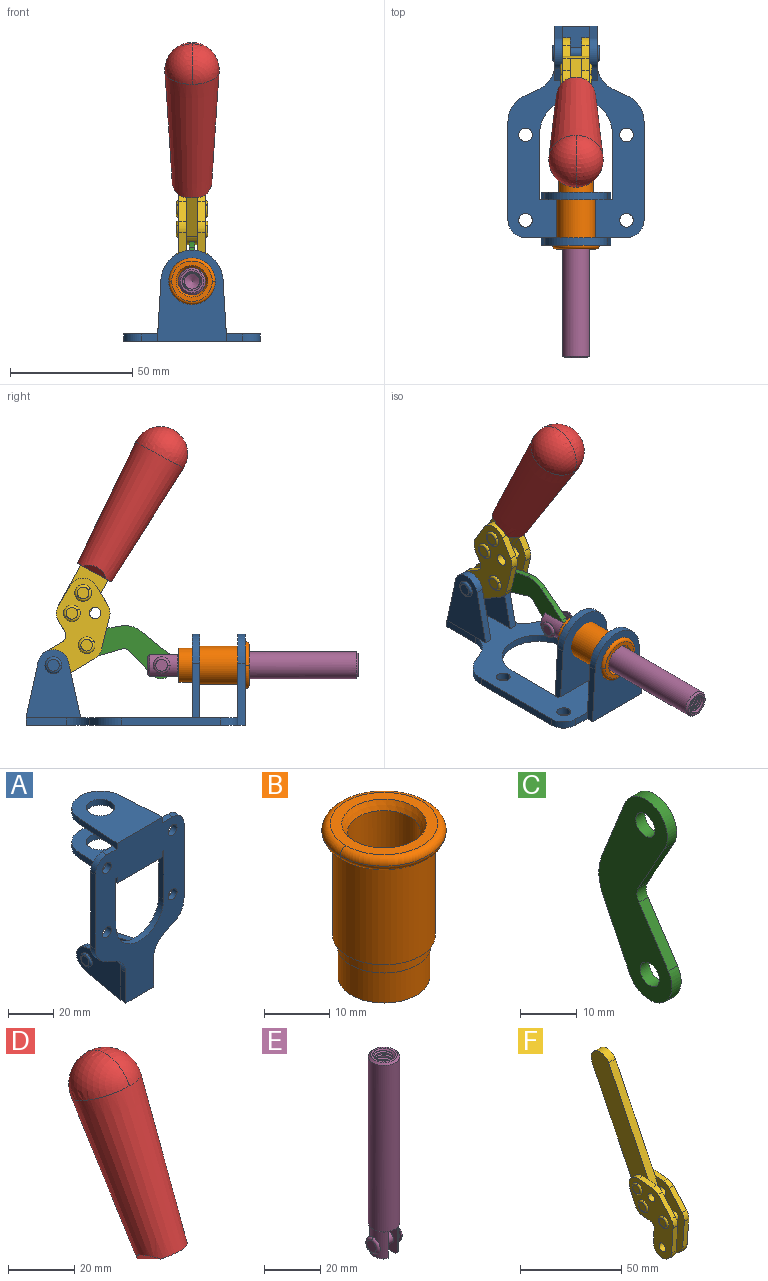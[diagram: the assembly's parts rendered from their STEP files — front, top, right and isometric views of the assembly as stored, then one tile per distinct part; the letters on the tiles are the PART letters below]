
ASSEMBLY  parts=6 mates=6
PART A: 55 faces, bbox 55.7x37.4x89.8 mm
  f0: torus R=2.41mm, axis (-1,0,0), area 15mm2, adj f11,f15,f25
  f1: torus R=2.41mm, axis (-1,0,0), area 15mm2, adj f10,f12,f22
  f2: cylinder r=2.78mm len=5.56mm, axis (0,-1,0), area 54.2mm2, adj f30,f54
  f3: cylinder r=14.99mm len=29.97mm, axis (0,-1,0), area 145.9mm2, adj f30,f49,f53,f54
  f4: cylinder r=2.78mm len=5.56mm, axis (0,-1,0), area 54.2mm2, adj f30,f54
  f5: cylinder r=2.78mm len=5.56mm, axis (0,-1,0), area 54.2mm2, adj f30,f54
  f6: cylinder r=2.78mm len=5.56mm, axis (0,-1,0), area 54.2mm2, adj f30,f54
  f7: cylinder r=6.35mm len=12.7mm, axis (0,0,1), area 123.6mm2, adj f27,f51
  f8: cylinder r=6.35mm len=12.7mm, axis (0,0,-1), area 124.7mm2, adj f21,f35
  f9: cylinder r=2.41mm len=11.18mm, axis (-1,0,0), area 169.4mm2, adj f16,f19
  f10: plane 4.83x4.83mm, normal (1,0,0), area 18.3mm2, adj f1,f12
  f11: plane 4.83x4.83mm, normal (-1,0,0), area 18.3mm2, adj f0,f15
  f12: torus R=2.41mm, axis (-1,0,0), area 15mm2, adj f1,f10,f22
  f13: cylinder r=6.35mm len=12.41mm, axis (1,0,0), area 53.4mm2, adj f18,f19,f22,f23
  f14: cylinder r=6.35mm len=12.41mm, axis (-1,0,0), area 53.4mm2, adj f16,f17,f24,f25
  f15: torus R=2.41mm, axis (-1,0,0), area 15mm2, adj f0,f11,f25
  f16: plane 27.86x22.35mm, normal (1,0,0), area 425.4mm2, adj f9,f14,f17,f24,f30
  f17: plane 22.86x4.97mm, normal (0,0.21,0.98), area 72.5mm2, adj f14,f16,f25,f30
  f18: plane 22.86x4.97mm, normal (0,0.21,0.98), area 72.5mm2, adj f13,f19,f22,f30
  f19: plane 27.86x22.35mm, normal (-1,0,0), area 425.4mm2, adj f9,f13,f18,f23,f30
  f20: cylinder r=12.7mm len=25.35mm, axis (0,0,-1), area 119.8mm2, adj f21,f34,f35,f36
  f21: plane 34.21x28.07mm, normal (0,0,-1), area 702.4mm2, adj f8,f20,f30,f34,f36
  f22: plane 27.96x22.45mm, normal (1,0,0), area 407.2mm2, adj f1,f12,f13,f18,f23,f30,f42,f43
  f23: plane 22.86x4.97mm, normal (0,0.21,-0.98), area 72.5mm2, adj f13,f19,f22,f44
  f24: plane 22.86x4.97mm, normal (0,0.21,-0.98), area 72.5mm2, adj f14,f16,f25,f44
  f25: plane 27.86x22.35mm, normal (-1,0,0), area 407.1mm2, adj f0,f14,f15,f17,f24,f30,f45,f46
  f26: plane 3.1x0.95mm, normal (0,0,-1), area 2.7mm2, adj f30,f49,f50,f54
  f27: plane 34.21x28.07mm, normal (0,0,1), area 702.4mm2, adj f7,f28,f30,f50,f52
  f28: cylinder r=12.7mm len=25.35mm, axis (0,0,1), area 118.8mm2, adj f27,f50,f51,f52
  f29: plane 3.1x0.95mm, normal (0,0,-1), area 2.7mm2, adj f30,f52,f53,f54
  f30: plane 86.54x55.63mm, normal (0,1,0), area 2362.9mm2, adj f2,f3,f4,f5,f6,f16,f17,f18
  f31: plane 40.56x3.1mm, normal (-1,0,0), area 125.7mm2, adj f30,f32,f48,f54
  f32: cylinder r=7.11mm len=7.11mm, axis (0,-1,0), area 34.6mm2, adj f30,f31,f33,f54
  f33: plane 6.67x3.1mm, normal (0,0,1), area 20.4mm2, adj f30,f32,f34,f54
  f34: plane 25.39x3.13mm, normal (-1,0.06,0), area 79.5mm2, adj f20,f21,f33,f35,f54
  f35: plane 37.31x28.45mm, normal (0,0,1), area 789.9mm2, adj f8,f20,f34,f36,f54
  f36: plane 25.39x3.13mm, normal (1,0.06,0), area 79.5mm2, adj f20,f21,f35,f37,f54
  f37: plane 6.67x3.1mm, normal (0,0,1), area 20.4mm2, adj f30,f36,f38,f54
  f38: cylinder r=7.11mm len=7.11mm, axis (0,-1,0), area 34.6mm2, adj f30,f37,f39,f54
  f39: plane 40.56x3.1mm, normal (1,0,0), area 125.7mm2, adj f30,f38,f40,f54
  f40: cylinder r=11.18mm len=10.16mm, axis (0,-1,0), area 39.5mm2, adj f30,f39,f41,f54
  f41: plane 6.09x3.1mm, normal (0.42,0,-0.91), area 20.8mm2, adj f30,f40,f42,f54
  f42: cylinder r=11.18mm len=9.41mm, axis (0,-1,0), area 37.2mm2, adj f22,f30,f41,f43,f54
  f43: plane 16.5x3.1mm, normal (1,0,0), area 51.1mm2, adj f22,f42,f44,f54
  f44: plane 17.37x3.1mm, normal (0,0,-1), area 53.8mm2, adj f23,f24,f30,f43,f45,f54
  f45: plane 16.5x3.1mm, normal (-1,0,0), area 51.1mm2, adj f25,f44,f46,f54
  f46: cylinder r=11.18mm len=9.41mm, axis (0,-1,0), area 37.2mm2, adj f25,f30,f45,f47,f54
  f47: plane 6.09x3.1mm, normal (-0.42,0,-0.91), area 20.8mm2, adj f30,f46,f48,f54
  f48: cylinder r=11.18mm len=10.16mm, axis (0,-1,0), area 39.5mm2, adj f30,f31,f47,f54
  f49: plane 26.54x3.1mm, normal (-1,0,0), area 82.3mm2, adj f3,f26,f30,f54
  f50: plane 25.39x3.1mm, normal (1,0.06,0), area 78.8mm2, adj f26,f27,f28,f51,f54
  f51: plane 37.31x28.45mm, normal (0,0,-1), area 789.9mm2, adj f7,f28,f50,f52,f54
  f52: plane 25.39x3.1mm, normal (-1,0.06,0), area 78.8mm2, adj f27,f28,f29,f51,f54
  f53: plane 26.54x3.1mm, normal (1,0,0), area 82.3mm2, adj f3,f29,f30,f54
  f54: plane 89.66x55.63mm, normal (0,-1,0), area 2678.5mm2, adj f2,f3,f4,f5,f6,f26,f29,f31
PART B: 15 faces, bbox 20.6x20.6x28.7 mm
  f0: torus R=8.26mm, axis (0,0,1), area 56.8mm2, adj f1,f10,f12
  f1: torus R=8.26mm, axis (0,0,1), area 56.8mm2, adj f0,f6,f13
  f2: cylinder r=5.59mm len=25.91mm, axis (0,0,1), area 909.6mm2, adj f3,f4
  f3: cone r=6.86mm half-angle=45deg, axis (0,0,-1), area 70.2mm2, adj f2,f14
  f4: cone r=6.47mm half-angle=30deg, axis (0,0,1), area 66.7mm2, adj f2,f13
  f5: cylinder r=7.04mm len=14.07mm, axis (0,0,1), area 252.6mm2, adj f11,f14
  f6: torus R=8.26mm, axis (0,0,1), area 56.8mm2, adj f1,f12,f13
  f7: cylinder r=7.16mm len=14.33mm, axis (0,0,1), area 91.5mm2, adj f9,f11
  f8: cylinder r=7.86mm len=18.42mm, axis (0,0,1), area 909.6mm2, adj f9,f10
  f9: plane 15.72x15.72mm, normal (0,0,-1), area 33mm2, adj f7,f8
  f10: plane 16.51x16.51mm, normal (0,0,-1), area 19.9mm2, adj f0,f8,f12
  f11: plane 14.33x14.33mm, normal (0,0,-1), area 5.7mm2, adj f5,f7
  f12: torus R=8.26mm, axis (0,0,1), area 56.8mm2, adj f0,f6,f10
  f13: plane 16.51x16.51mm, normal (0,0,1), area 82.7mm2, adj f1,f4,f6
  f14: plane 14.07x14.07mm, normal (0,0,-1), area 7.8mm2, adj f3,f5
PART C: 12 faces, bbox 2.3x18.2x42.8 mm
  f0: cylinder r=2.4mm len=4.8mm, axis (1,0,0), area 34.9mm2, adj f4,f11
  f1: cylinder r=10.41mm len=8.47mm, axis (1,0,0), area 20.2mm2, adj f4,f9,f10,f11
  f2: cylinder r=3.05mm len=3.16mm, axis (1,0,0), area 7.7mm2, adj f4,f6,f7,f11
  f3: cylinder r=2.4mm len=4.8mm, axis (1,0,0), area 34.9mm2, adj f4,f11
  f4: plane 42.81x18.23mm, normal (-1,0,0), area 414.1mm2, adj f0,f1,f2,f3,f5,f6,f7,f8
  f5: cylinder r=5.54mm len=10.67mm, axis (1,0,0), area 41.8mm2, adj f4,f6,f10,f11
  f6: plane 11.66x6.53mm, normal (0,-0.87,-0.49), area 30.9mm2, adj f2,f4,f5,f11
  f7: plane 11.17x7.33mm, normal (0,-0.84,0.55), area 30.9mm2, adj f2,f4,f8,f11
  f8: cylinder r=5.54mm len=10.51mm, axis (1,0,0), area 41.8mm2, adj f4,f7,f9,f11
  f9: plane 13.67x6.67mm, normal (0,0.9,-0.44), area 35.1mm2, adj f1,f4,f8,f11
  f10: plane 14.1x5.7mm, normal (0,0.93,0.37), area 35.1mm2, adj f1,f4,f5,f11
  f11: plane 42.81x18.23mm, normal (1,0,0), area 414.1mm2, adj f0,f1,f2,f3,f5,f6,f7,f8
PART D: 11 faces, bbox 22.3x42.6x64.5 mm
  f0: sphere r=11.13mm, area 411.4mm2, adj f1,f8
  f1: cone r=11.11mm half-angle=3.3deg, axis (0,0.44,0.9), area 3251.8mm2, adj f0,f7,f8,f9,f10
  f2: cylinder r=6.16mm len=11.7mm, axis (1,0,0), area 89.5mm2, adj f3,f4,f5,f6
  f3: plane 60.23x36.75mm, normal (-1,0,0), area 763.6mm2, adj f2,f4,f6,f10
  f4: plane 51.37x25.05mm, normal (0,0.9,-0.44), area 264.2mm2, adj f2,f3,f5,f10
  f5: plane 60.23x36.75mm, normal (1,0,0), area 763.6mm2, adj f2,f4,f6,f10
  f6: plane 51.37x25.05mm, normal (0,-0.9,0.44), area 264.2mm2, adj f2,f3,f5,f10
  f7: plane 9.95x5.95mm, normal (0.71,-0.31,-0.64), area 25.8mm2, adj f1,f10
  f8: sphere r=11.13mm, area 411.4mm2, adj f0,f1
  f9: plane 9.95x5.95mm, normal (-0.71,-0.31,-0.64), area 25.8mm2, adj f1,f10
  f10: plane 14.27x11.38mm, normal (0,-0.44,-0.9), area 106.7mm2, adj f1,f3,f4,f5,f6,f7,f9
PART E: 48 faces, bbox 12.6x11.1x86.1 mm
  f0: torus R=2.41mm, axis (-1,0,0), area 15mm2, adj f30,f32,f34
  f1: torus R=2.41mm, axis (-1,0,0), area 15mm2, adj f29,f31,f33
  f2: cylinder r=5.54mm len=72.39mm, axis (0,0,1), area 2518.5mm2, adj f3,f4,f42,f43
  f3: cone r=5.54mm half-angle=45deg, axis (0,0,1), area 7.6mm2, adj f2,f5,f41
  f4: cone r=5.54mm half-angle=45deg, axis (0,0,-1), area 34.9mm2, adj f2,f39
  f5: cylinder r=5.08mm len=11.48mm, axis (0,0,1), area 108.3mm2, adj f3,f7,f8,f41
  f6: cylinder r=2.41mm len=4.83mm, axis (-1,0,0), area 71.2mm2, adj f40,f41
  f7: cylinder r=2.41mm len=4.83mm, axis (-1,0,0), area 7.6mm2, adj f5,f34
  f8: cone r=5.08mm half-angle=45deg, axis (0,0,1), area 10.6mm2, adj f5,f37,f41
  f9: cone r=3.98mm half-angle=45deg, axis (0,0,1), area 17.6mm2, adj f27,f39,f45,f46,f47
  f10: cylinder r=2.41mm len=4.83mm, axis (-1,0,0), area 7.6mm2, adj f33,f38
  f11: cylinder r=3.2mm len=6.4mm, axis (0,0,1), area 78.4mm2, adj f12,f28,f44,f45,f47
  f12: cylinder r=3.2mm len=6.4mm, axis (0,0,1), area 10.5mm2, adj f11,f13,f45,f47
  f13: cylinder r=3.2mm len=6.4mm, axis (0,0,1), area 10.5mm2, adj f12,f14,f45,f47
  f14: cylinder r=3.2mm len=6.4mm, axis (0,0,1), area 10.5mm2, adj f13,f15,f45,f47
  f15: cylinder r=3.2mm len=6.4mm, axis (0,0,1), area 10.5mm2, adj f14,f16,f45,f47
  f16: cylinder r=3.2mm len=6.4mm, axis (0,0,1), area 10.5mm2, adj f15,f17,f45,f47
  f17: cylinder r=3.2mm len=6.4mm, axis (0,0,1), area 10.5mm2, adj f16,f18,f45,f47
  f18: cylinder r=3.2mm len=6.4mm, axis (0,0,1), area 10.5mm2, adj f17,f19,f45,f47
  f19: cylinder r=3.2mm len=6.4mm, axis (0,0,1), area 10.5mm2, adj f18,f20,f45,f47
  f20: cylinder r=3.2mm len=6.4mm, axis (0,0,1), area 10.5mm2, adj f19,f21,f45,f47
  f21: cylinder r=3.2mm len=6.4mm, axis (0,0,1), area 10.5mm2, adj f20,f22,f45,f47
  f22: cylinder r=3.2mm len=6.4mm, axis (0,0,1), area 10.5mm2, adj f21,f23,f45,f47
  f23: cylinder r=3.2mm len=6.4mm, axis (0,0,1), area 10.5mm2, adj f22,f24,f45,f47
  f24: cylinder r=3.2mm len=6.4mm, axis (0,0,1), area 10.5mm2, adj f23,f25,f45,f47
  f25: cylinder r=3.2mm len=6.4mm, axis (0,0,1), area 10.5mm2, adj f24,f26,f45,f47
  f26: cylinder r=3.2mm len=6.4mm, axis (0,0,1), area 10.5mm2, adj f25,f27,f45,f47
  f27: cylinder r=3.2mm len=6.4mm, axis (0,0,1), area 7.4mm2, adj f9,f26,f45,f47
  f28: cone r=3.2mm half-angle=60deg, axis (0,0,1), area 37.2mm2, adj f11
  f29: plane 4.83x4.83mm, normal (-1,0,0), area 18.3mm2, adj f1,f31
  f30: plane 4.83x4.83mm, normal (1,0,0), area 18.3mm2, adj f0,f32
  f31: torus R=2.41mm, axis (-1,0,0), area 15mm2, adj f1,f29,f33
  f32: torus R=2.41mm, axis (-1,0,0), area 15mm2, adj f0,f30,f34
  f33: plane 6.83x6.83mm, normal (1,0,0), area 18.3mm2, adj f1,f10,f31
  f34: plane 6.83x6.83mm, normal (-1,0,0), area 18.3mm2, adj f0,f7,f32
  f35: cone r=5.08mm half-angle=45deg, axis (0,0,1), area 10.6mm2, adj f36,f38,f40
  f36: plane 7.25x1.97mm, normal (0,0,-1), area 10mm2, adj f35,f40
  f37: plane 7.25x1.97mm, normal (0,0,-1), area 10mm2, adj f8,f41
  f38: cylinder r=5.08mm len=11.48mm, axis (0,0,1), area 108.3mm2, adj f10,f35,f40,f42
  f39: plane 9.55x9.55mm, normal (0,0,1), area 22mm2, adj f4,f9
  f40: plane 12.76x10.09mm, normal (1,0,0), area 95.7mm2, adj f6,f35,f36,f38,f42,f43
  f41: plane 12.76x10.09mm, normal (-1,0,0), area 95.7mm2, adj f3,f5,f6,f8,f37,f43
  f42: cone r=5.54mm half-angle=45deg, axis (0,0,1), area 7.6mm2, adj f2,f38,f40
  f43: plane 11.07x4.7mm, normal (0,0,-1), area 50.4mm2, adj f2,f40,f41
  f44: plane 0.89x0.62mm, normal (-1,0,0), area 0.3mm2, adj f11,f45,f46,f47
  f45: bspline ~24.8x7.63mm, area 266.6mm2, adj f9,f11,f12,f13,f14,f15,f16,f17
  f46: bspline ~24.87x7.63mm, area 73.6mm2, adj f9,f44,f45,f47
  f47: bspline ~24.98x7.63mm, area 272.5mm2, adj f9,f11,f12,f13,f14,f15,f16,f17
PART F: 59 faces, bbox 12.9x60.2x99.6 mm
  f0: torus R=2.39mm, axis (-1,0,0), area 14.9mm2, adj f20,f43,f51
  f1: torus R=2.39mm, axis (-1,0,0), area 14.9mm2, adj f19,f42,f51
  f2: torus R=2.39mm, axis (-1,0,0), area 14.9mm2, adj f18,f35,f51
  f3: torus R=2.39mm, axis (-1,0,0), area 14.9mm2, adj f14,f17,f23
  f4: torus R=2.39mm, axis (-1,0,0), area 14.9mm2, adj f13,f16,f23
  f5: torus R=2.39mm, axis (-1,0,0), area 14.9mm2, adj f12,f15,f23
  f6: cylinder r=2.39mm len=4.78mm, axis (1,0,0), area 46.5mm2, adj f48,f50,f51
  f7: cylinder r=2.39mm len=4.78mm, axis (1,0,0), area 46.5mm2, adj f50,f51
  f8: cylinder r=6.35mm len=12.68mm, axis (1,0,0), area 61.8mm2, adj f38,f39,f50,f51
  f9: cylinder r=2.39mm len=4.78mm, axis (-1,0,0), area 70.5mm2, adj f46,f50
  f10: cylinder r=2.39mm len=4.78mm, axis (-1,0,0), area 46.5mm2, adj f23,f45,f46
  f11: cylinder r=2.39mm len=4.78mm, axis (-1,0,0), area 46.5mm2, adj f23,f46
  f12: plane 4.78x4.78mm, normal (1,0,0), area 17.9mm2, adj f5,f15
  f13: plane 4.78x4.78mm, normal (1,0,0), area 17.9mm2, adj f4,f16
  f14: plane 4.78x4.78mm, normal (1,0,0), area 17.9mm2, adj f3,f17
  f15: torus R=2.39mm, axis (-1,0,0), area 14.9mm2, adj f5,f12,f23
  f16: torus R=2.39mm, axis (-1,0,0), area 14.9mm2, adj f4,f13,f23
  f17: torus R=2.39mm, axis (-1,0,0), area 14.9mm2, adj f3,f14,f23
  f18: plane 4.78x4.78mm, normal (-1,0,0), area 17.9mm2, adj f2,f35
  f19: plane 4.78x4.78mm, normal (-1,0,0), area 17.9mm2, adj f1,f42
  f20: plane 4.78x4.78mm, normal (-1,0,0), area 17.9mm2, adj f0,f43
  f21: plane 2.26x0.2mm, normal (1,0,0), area 0.2mm2, adj f31,f44
  f22: plane 2.26x0.2mm, normal (-1,0,0), area 0.2mm2, adj f41,f44
  f23: plane 39.37x30.77mm, normal (1,0,0), area 565.5mm2, adj f3,f4,f5,f10,f11,f15,f16,f17
  f24: cylinder r=6.1mm len=4.15mm, axis (-1,0,0), area 14.7mm2, adj f23,f25,f32,f46
  f25: plane 10.25x9.01mm, normal (0,-0.75,0.66), area 42.3mm2, adj f23,f24,f26,f46
  f26: cylinder r=6.35mm len=4.64mm, axis (-1,0,0), area 15.6mm2, adj f23,f25,f27,f46
  f27: plane 15.84x3.1mm, normal (0,-1,-0.07), area 49.2mm2, adj f23,f26,f28,f46
  f28: cylinder r=6.35mm len=12.68mm, axis (-1,0,0), area 61.8mm2, adj f23,f27,f29,f46
  f29: plane 8.11x3.1mm, normal (0,1,0.07), area 25.2mm2, adj f23,f28,f30,f46
  f30: cylinder r=3.05mm len=3.25mm, axis (-1,0,0), area 14.8mm2, adj f23,f29,f31,f46
  f31: plane 5.99x3.1mm, normal (0,0.07,-1), area 18.6mm2, adj f21,f23,f30,f44,f46
  f32: plane 9.5x3.1mm, normal (0,-0.07,1), area 29.5mm2, adj f23,f24,f33,f46,f47
  f33: cylinder r=6.1mm len=8.63mm, axis (-1,0,0), area 39.1mm2, adj f23,f32,f34,f47
  f34: plane 8.65x3.96mm, normal (0,0.91,-0.42), area 29.5mm2, adj f23,f33,f44,f47
  f35: torus R=2.39mm, axis (-1,0,0), area 14.9mm2, adj f2,f18,f51
  f36: plane 10.25x9.01mm, normal (0,-0.75,0.66), area 42.3mm2, adj f37,f49,f50,f51
  f37: cylinder r=6.35mm len=4.64mm, axis (1,0,0), area 15.6mm2, adj f36,f38,f50,f51
  f38: plane 15.84x3.1mm, normal (0,-1,-0.07), area 49.2mm2, adj f8,f37,f50,f51
  f39: plane 8.11x3.1mm, normal (0,1,0.07), area 25.2mm2, adj f8,f40,f50,f51
  f40: cylinder r=3.05mm len=3.25mm, axis (1,0,0), area 14.8mm2, adj f39,f41,f50,f51
  f41: plane 5.99x3.1mm, normal (0,0.07,-1), area 18.6mm2, adj f22,f40,f44,f50,f51
  f42: torus R=2.39mm, axis (-1,0,0), area 14.9mm2, adj f1,f19,f51
  f43: torus R=2.39mm, axis (-1,0,0), area 14.9mm2, adj f0,f20,f51
  f44: cylinder r=6.35mm len=12.12mm, axis (-1,0,0), area 128.9mm2, adj f21,f22,f23,f31,f34,f41,f46,f47
  f45: plane 2.65x1.35mm, normal (1,0,0), area 1mm2, adj f10,f55
  f46: plane 39.08x20.42mm, normal (-1,0,0), area 412.5mm2, adj f9,f10,f11,f24,f25,f26,f27,f28
  f47: plane 77.62x39.82mm, normal (1,0,0), area 850mm2, adj f32,f33,f34,f44,f53,f54,f55
  f48: plane 2.65x1.35mm, normal (-1,0,0), area 1mm2, adj f6,f55
  f49: cylinder r=6.1mm len=4.15mm, axis (1,0,0), area 14.7mm2, adj f36,f50,f51,f56
  f50: plane 39.08x20.42mm, normal (1,0,0), area 412.5mm2, adj f6,f7,f8,f9,f36,f37,f38,f39
  f51: plane 39.37x30.77mm, normal (-1,0,0), area 565.5mm2, adj f0,f1,f2,f6,f7,f8,f35,f36
  f52: plane 8.65x3.96mm, normal (0,0.91,-0.42), area 29.5mm2, adj f44,f51,f57,f58
  f53: plane 68.49x33.4mm, normal (0,0.9,-0.44), area 358.1mm2, adj f44,f47,f54,f58
  f54: cylinder r=6.35mm len=12.06mm, axis (1,0,0), area 93.7mm2, adj f47,f53,f55,f58
  f55: plane 68.49x33.4mm, normal (0,-0.9,0.44), area 358.1mm2, adj f44,f45,f46,f47,f48,f50,f54,f58
  f56: plane 9.5x3.1mm, normal (0,-0.07,1), area 29.5mm2, adj f49,f50,f51,f57,f58
  f57: cylinder r=6.1mm len=8.63mm, axis (1,0,0), area 39.1mm2, adj f51,f52,f56,f58
  f58: plane 77.62x39.82mm, normal (-1,0,0), area 850mm2, adj f44,f52,f53,f54,f55,f56,f57
PLACE A rot(axis=(1,0,0),90deg) t=(0,9.43,0)mm fixed
PLACE B rot(axis=(1,0,0),90deg) t=(0,10.45,0)mm
PLACE C rot(axis=(1,0,0),106.9deg) t=(0,19.2,5.57)mm
PLACE D rot(axis=(1,0,0),55deg) t=(0,1.12,22.86)mm
PLACE E rot(axis=(1,0,0),90deg) t=(0,12.71,0)mm
PLACE F rot(axis=(1,0,0),55deg) t=(0,1.12,22.86)mm
MATE fastened D.f2 <-> F.f54  axis (1,0,0) through (0,-3,112.47)mm
MATE revolute F.f7 <-> A.f0  axis (-1,0,0) through (0,41.52,24.61)mm
MATE slider A.f7 <-> E.f2  axis (0,-1,0) through (0,-36.96,24.61)mm
MATE revolute C.f3 <-> F.f4  axis (1,0,0) through (0,27.92,32.79)mm
MATE fastened B.f2 <-> A.f7  axis (0,-1,0) through (0,-36.96,24.61)mm
MATE revolute E.f6 <-> C.f5  axis (-1,0,0) through (0,-2.76,24.61)mm
